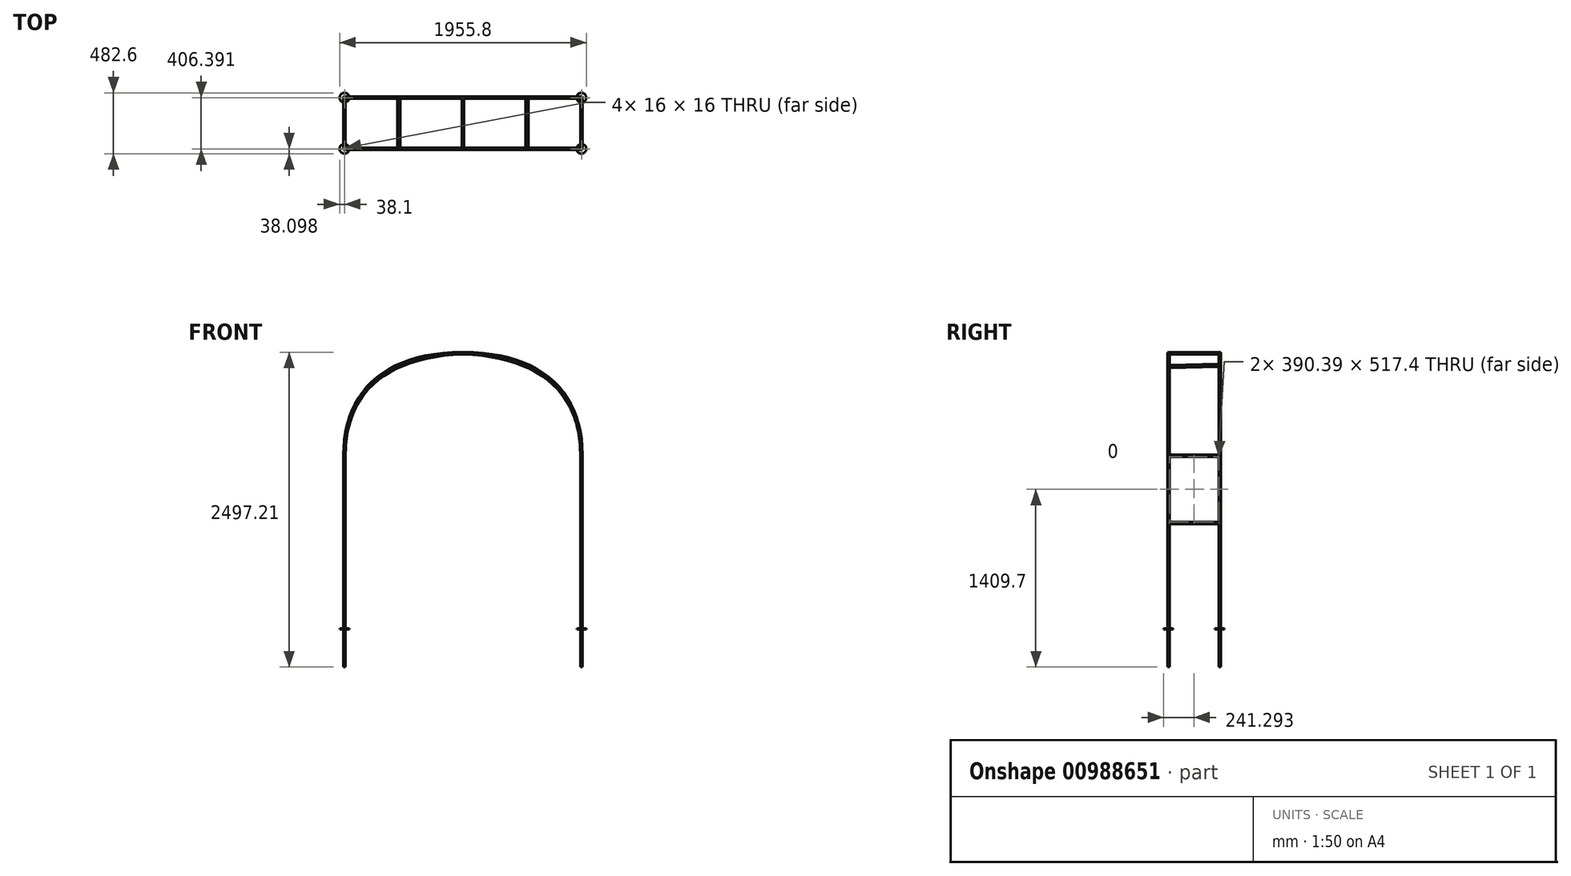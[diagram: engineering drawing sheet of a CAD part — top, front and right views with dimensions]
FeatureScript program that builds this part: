
annotation { "Feature Type Name" : "Feature", "Feature Type Description" : "" }
export const myFeature = defineFeature(function(context is Context, id is Id, definition is map)
    precondition{}
    {
        {
            var Q0;
            Q0=qCreatedBy(makeId("Right.planeOp"),FACE);
            cPlane(context, id + "F0", {"entities" : qUnion([Q0]), "cplaneType" : CPlaneType.OFFSET, "offset" : 939.8 * mm, "oppositeDirection" : true, "width" : 152.4 * mm, "height" : 152.4 * mm});
        }
        {
            var Q0;
            Q0=qCreatedBy(id+"F0.planeOp",FACE);
            var sketch = newSketch(context, id + "F1", { "sketchPlane" : qUnion([Q0])});
            skLineSegment(sketch, "E0", {"start": v(0, 0) * mm, "end": v(-203.2, 0) * mm, "construction": true});
            skLineSegment(sketch, "E1", {"start": v(0, 0) * mm, "end": v(203.2, 0) * mm, "construction": true});
            skLineSegment(sketch, "E2", {"start": v(203.2, 0) * mm, "end": v(203.2, 2184.4) * mm, "construction": true});
            skLineSegment(sketch, "E3", {"start": v(203.2, 2184.4) * mm, "end": v(-203.2, 2184.4) * mm, "construction": true});
            skLineSegment(sketch, "E4", {"start": v(-203.2, 2184.4) * mm, "end": v(-203.2, 0) * mm, "construction": true});
            skSolve(sketch);
        }
        {
            var Q0;
            Q0=qCreatedBy(makeId("Right.planeOp"),FACE);
            var sketch = newSketch(context, id + "F2", { "sketchPlane" : qUnion([Q0])});
            skPoint(sketch, "E5.0", {"position": v(0, 2184.4) * mm});
            skLineSegment(sketch, "E6.0", {"start": v(-203.2, 2184.4) * mm, "end": v(-203.2, 0) * mm, "construction": true});
            skLineSegment(sketch, "E7.0", {"start": v(203.2, 0) * mm, "end": v(203.2, 2184.4) * mm, "construction": true});
            skSolve(sketch);
        }
        {
            var Q0;
            Q0=qCreatedBy(id+"F0.planeOp",FACE);
            var sketch = newSketch(context, id + "F3", { "sketchPlane" : qUnion([Q0])});
            skLineSegment(sketch, "E8", {"start": v(-203.2, 0) * mm, "end": v(-203.2, 1371.6) * mm});
            skLineSegment(sketch, "E9", {"start": v(203.19, 0) * mm, "end": v(203.19, 1371.6) * mm});
            skSolve(sketch);
        }
        {
            var Q0;
            Q0=sQuery(id+"F1.wireOp",EDGE,"E4");
            cPlane(context, id + "F4", {"entities" : qUnion([Q0]), "cplaneType" : CPlaneType.LINE_ANGLE, "offset" : 25.4 * mm, "angle" : 90 * degree, "width" : 152.4 * mm, "height" : 152.4 * mm});
        }
        {
            var Q0;
            Q0=sQuery(id+"F1.wireOp",EDGE,"E2");
            cPlane(context, id + "F5", {"entities" : qUnion([Q0]), "cplaneType" : CPlaneType.LINE_ANGLE, "offset" : 25.4 * mm, "angle" : 90 * degree, "width" : 152.4 * mm, "height" : 152.4 * mm});
        }
        {
            var Q0;
            Q0=qCreatedBy(id+"F4.planeOp",FACE);
            var sketch = newSketch(context, id + "F6", { "sketchPlane" : qUnion([Q0])});
            skFitSpline(sketch, "E10", {"points": [v(939.8, 1371.6) * mm, v(0, 2184.4) * mm], "startDerivative": vector(-1.02, 1524) * mm, "endDerivative": vector(-1828.8, 68.52) * mm});
            skLineSegment(sketch, "E11", {"start": v(609.6, 2161.56) * mm, "end": v(0, 2184.4) * mm, "construction": true});
            skLineSegment(sketch, "E12", {"start": v(939.8, 1371.6) * mm, "end": v(939.46, 1879.6) * mm, "construction": true});
            skSolve(sketch);
        }
        {
            var Q0;
            Q0=qCreatedBy(id+"F5.planeOp",FACE);
            var sketch = newSketch(context, id + "F7", { "sketchPlane" : qUnion([Q0])});
            skFitSpline(sketch, "E13", {"points": [v(939.8, 1371.6) * mm, v(0, 2184.4) * mm], "startDerivative": vector(3.24, 1524) * mm, "endDerivative": vector(-1828.8, -5.61) * mm});
            skLineSegment(sketch, "E14", {"start": v(939.8, 1371.6) * mm, "end": v(940.88, 1879.6) * mm, "construction": true});
            skLineSegment(sketch, "E15", {"start": v(0, 2184.4) * mm, "end": v(609.6, 2186.27) * mm, "construction": true});
            skSolve(sketch);
        }
        {
            var Q0;
            Q0=qCreatedBy(makeId("Top.planeOp"),FACE);
            var sketch = newSketch(context, id + "F8", { "sketchPlane" : qUnion([Q0])});
            skLineSegment(sketch, "E16.bottom", {"start": v(-947.8, -195.2) * mm, "end": v(-931.8, -195.2) * mm});
            skLineSegment(sketch, "E16.top", {"start": v(-947.8, -211.2) * mm, "end": v(-931.8, -211.2) * mm});
            skLineSegment(sketch, "E16.left", {"start": v(-947.8, -195.2) * mm, "end": v(-947.8, -211.2) * mm});
            skLineSegment(sketch, "E16.right", {"start": v(-931.8, -195.2) * mm, "end": v(-931.8, -211.2) * mm});
            skLineSegment(sketch, "E17", {"start": v(-947.8, -195.2) * mm, "end": v(-931.8, -211.2) * mm, "construction": true});
            skPoint(sketch, "E18", {"position": v(-939.8, -203.2) * mm});
            skLineSegment(sketch, "E19.bottom", {"start": v(-931.8, 211.19) * mm, "end": v(-947.8, 211.19) * mm});
            skLineSegment(sketch, "E19.top", {"start": v(-931.8, 195.19) * mm, "end": v(-947.8, 195.19) * mm});
            skLineSegment(sketch, "E19.left", {"start": v(-931.8, 211.19) * mm, "end": v(-931.8, 195.19) * mm});
            skLineSegment(sketch, "E19.right", {"start": v(-947.8, 211.19) * mm, "end": v(-947.8, 195.19) * mm});
            skLineSegment(sketch, "E20", {"start": v(-931.8, 211.19) * mm, "end": v(-947.8, 195.19) * mm, "construction": true});
            skPoint(sketch, "E21", {"position": v(-939.8, 203.19) * mm});
            skSolve(sketch);
        }
        {
            var Q0;
            Q0=makeQuery(id+"F8.imprint","IMPRINT",FACE,{"disambiguationData":[TD([[makeQuery(id+"F8.imprint","IMPRINT",EDGE,{"derivedFrom":sQuery(id+"F8.wireOp",EDGE,"E19.bottom")}),1.0]])]});
            var Q1;
            Q1=sQuery(id+"F3.wireOp",EDGE,"E9");
            sweep(context, id + "F9", {"profiles" : qUnion([Q0]), "path" : qUnion([Q1])});
        }
        {
            var Q0;
            Q0=makeQuery(id+"F8.imprint","IMPRINT",FACE,{"disambiguationData":[TD([[makeQuery(id+"F8.imprint","IMPRINT",EDGE,{"derivedFrom":sQuery(id+"F8.wireOp",EDGE,"E16.bottom")}),-1.0]])]});
            var Q1;
            Q1=sQuery(id+"F3.wireOp",EDGE,"E8");
            sweep(context, id + "F10", {"profiles" : qUnion([Q0]), "path" : qUnion([Q1])});
        }
        {
            var Q0;
            Q0=makeQuery(id+"F10.opSweep","CAP_FACE",FACE,{"disambiguationData":[OSD([sQuery(id+"F3.wireOp",VERTEX,"E8.end"),sQuery(id+"F8.wireOp",EDGE,"dGPdL38b-pFhj-TtEV-cKe8-G57E5a3NYJfa")])],"isStart":false});
            var Q1;
            Q1=sQuery(id+"F6.wireOp",EDGE,"E10");
            sweep(context, id + "F11", {"operationType" : NewBodyOperationType.ADD, "profiles" : qUnion([Q0]), "path" : qUnion([Q1])});
        }
        {
            var Q0;
            Q0=qCreatedBy(id+"F0.planeOp",FACE);
            var sketch = newSketch(context, id + "F12", { "sketchPlane" : qUnion([Q0])});
            skLineSegment(sketch, "E22", {"start": v(203.19, 838.2) * mm, "end": v(-203.2, 838.2) * mm});
            skSolve(sketch);
        }
        {
            var Q0;
            Q0=qCreatedBy(id+"F0.planeOp",FACE);
            var sketch = newSketch(context, id + "F13", { "sketchPlane" : qUnion([Q0])});
            skLineSegment(sketch, "E23", {"start": v(-203.2, 1371.6) * mm, "end": v(203.19, 1371.6) * mm});
            skSolve(sketch);
        }
        {
            var Q0;
            Q0=makeQuery(id+"F9.opSweep","CAP_FACE",FACE,{"disambiguationData":[OSD([sQuery(id+"F3.wireOp",VERTEX,"E9.end"),sQuery(id+"F8.wireOp",EDGE,"A7kbO7hZ-qHPU-M1P2-TBv8-yGFhnXoMKm63")])],"isStart":false});
            var Q1;
            Q1=sQuery(id+"F7.wireOp",EDGE,"E13");
            sweep(context, id + "F14", {"operationType" : NewBodyOperationType.ADD, "profiles" : qUnion([Q0]), "path" : qUnion([Q1])});
        }
        {
            var Q0;
            Q0=qCreatedBy(makeId("Right.planeOp"),FACE);
            var sketch = newSketch(context, id + "F15", { "sketchPlane" : qUnion([Q0])});
            skLineSegment(sketch, "E24", {"start": v(-203.2, 2184.4) * mm, "end": v(203.2, 2184.4) * mm});
            skSolve(sketch);
        }
        {
            var Q0;
            Q0=qCreatedBy(id+"F4.planeOp",FACE);
            var sketch = newSketch(context, id + "F16", { "sketchPlane" : qUnion([Q0])});
            skCircle(sketch, "E25", {"center": v(939.8, 838.2) * mm, "radius": 8 * mm});
            skCircle(sketch, "E26", {"center": v(939.8, 1371.6) * mm, "radius": 8 * mm});
            skLineSegment(sketch, "E27.bottom", {"start": v(947.8, 830.2) * mm, "end": v(931.8, 830.2) * mm});
            skLineSegment(sketch, "E27.top", {"start": v(947.8, 846.2) * mm, "end": v(931.8, 846.2) * mm});
            skLineSegment(sketch, "E27.left", {"start": v(947.8, 830.2) * mm, "end": v(947.8, 846.2) * mm});
            skLineSegment(sketch, "E27.right", {"start": v(931.8, 830.2) * mm, "end": v(931.8, 846.2) * mm});
            skLineSegment(sketch, "E28", {"start": v(947.8, 830.2) * mm, "end": v(931.8, 846.2) * mm, "construction": true});
            skLineSegment(sketch, "E29.bottom", {"start": v(947.8, 1379.6) * mm, "end": v(931.8, 1379.6) * mm});
            skLineSegment(sketch, "E29.top", {"start": v(947.8, 1363.6) * mm, "end": v(931.8, 1363.6) * mm});
            skLineSegment(sketch, "E29.left", {"start": v(947.8, 1379.6) * mm, "end": v(947.8, 1363.6) * mm});
            skLineSegment(sketch, "E29.right", {"start": v(931.8, 1379.6) * mm, "end": v(931.8, 1363.6) * mm});
            skLineSegment(sketch, "E30", {"start": v(947.8, 1363.6) * mm, "end": v(931.8, 1379.6) * mm, "construction": true});
            skSolve(sketch);
        }
        {
            var Q0;
            Q0=makeQuery(id+"F16.imprint","IMPRINT",FACE,{"disambiguationData":[TD([[makeQuery(id+"F16.imprint","IMPRINT",EDGE,{"derivedFrom":sQuery(id+"F16.wireOp",EDGE,"E25")}),1.0]])]});
            var Q1;
            Q1=sQuery(id+"F12.wireOp",EDGE,"E22");
            sweep(context, id + "F17", {"operationType" : NewBodyOperationType.ADD, "profiles" : qUnion([Q0]), "path" : qUnion([Q1])});
        }
        {
            var Q0;
            Q0=qSketchRegion(id+"F16",true);
            var Q1;
            Q1=sQuery(id+"F13.wireOp",EDGE,"E23");
            sweep(context, id + "F18", {"operationType" : NewBodyOperationType.ADD, "profiles" : qUnion([Q0]), "path" : qUnion([Q1])});
        }
        {
            var Q0;
            Q0=qCreatedBy(id+"F4.planeOp",FACE);
            var sketch = newSketch(context, id + "F19", { "sketchPlane" : qUnion([Q0])});
            skLineSegment(sketch, "E31", {"start": v(8, 2176.4) * mm, "end": v(-8, 2192.4) * mm, "construction": true});
            skPoint(sketch, "E32", {"position": v(0, 2184.4) * mm});
            skLineSegment(sketch, "E33.bottom", {"start": v(8, 2176.4) * mm, "end": v(-8, 2176.4) * mm});
            skLineSegment(sketch, "E33.top", {"start": v(8, 2192.4) * mm, "end": v(-8, 2192.4) * mm});
            skLineSegment(sketch, "E33.left", {"start": v(8, 2176.4) * mm, "end": v(8, 2192.4) * mm});
            skLineSegment(sketch, "E33.right", {"start": v(-8, 2176.4) * mm, "end": v(-8, 2192.4) * mm});
            skSolve(sketch);
        }
        {
            var Q0;
            Q0=makeQuery(id+"F19.imprint","IMPRINT",FACE,{"disambiguationData":[TD([[makeQuery(id+"F19.imprint","IMPRINT",EDGE,{"derivedFrom":sQuery(id+"F19.wireOp",EDGE,"E33.bottom")}),-1.0]])]});
            var Q1;
            Q1=sQuery(id+"F15.wireOp",EDGE,"E24");
            sweep(context, id + "F20", {"operationType" : NewBodyOperationType.ADD, "profiles" : qUnion([Q0]), "path" : qUnion([Q1])});
        }
        {
            var Q0;
            Q0=qCreatedBy(makeId("Right.planeOp"),FACE);
            cPlane(context, id + "F21", {"entities" : qUnion([Q0]), "cplaneType" : CPlaneType.OFFSET, "offset" : 508 * mm, "oppositeDirection" : true, "width" : 152.4 * mm, "height" : 152.4 * mm});
        }
        {
            var Q0;
            Q0=qCreatedBy(id+"F21.planeOp",FACE);
            var sketch = newSketch(context, id + "F22", { "sketchPlane" : qUnion([Q0])});
            skLineSegment(sketch, "E34", {"start": v(-203.2, 2079.37) * mm, "end": v(203.05, 2090.49) * mm});
            skSolve(sketch);
        }
        {
            var Q0;
            Q0=qCreatedBy(id+"F4.planeOp",FACE);
            var sketch = newSketch(context, id + "F23", { "sketchPlane" : qUnion([Q0])});
            skLineSegment(sketch, "E35.bottom", {"start": v(518.22, 2082.18) * mm, "end": v(503.72, 2088.94) * mm});
            skLineSegment(sketch, "E35.top", {"start": v(511.46, 2067.67) * mm, "end": v(496.96, 2074.44) * mm});
            skLineSegment(sketch, "E35.left", {"start": v(518.22, 2082.18) * mm, "end": v(511.46, 2067.67) * mm});
            skLineSegment(sketch, "E35.right", {"start": v(503.72, 2088.94) * mm, "end": v(496.96, 2074.44) * mm});
            skPoint(sketch, "E36", {"position": v(507.59, 2078.3) * mm});
            skLineSegment(sketch, "E37", {"start": v(511.46, 2067.67) * mm, "end": v(503.72, 2088.94) * mm, "construction": true});
            skSolve(sketch);
        }
        {
            var Q0;
            Q0=qSketchRegion(id+"F23",true);
            var Q1;
            Q1=sQuery(id+"F22.wireOp",EDGE,"E34");
            sweep(context, id + "F24", {"operationType" : NewBodyOperationType.ADD, "profiles" : qUnion([Q0]), "path" : qUnion([Q1])});
        }
        {
            var Q0;
            Q0=qCreatedBy(makeId("Top.planeOp"),FACE);
            var sketch = newSketch(context, id + "F25", { "sketchPlane" : qUnion([Q0])});
            skCircle(sketch, "E38", {"center": v(-939.8, -203.2) * mm, "radius": 38.1 * mm});
            skCircle(sketch, "E39", {"center": v(-939.8, 203.2) * mm, "radius": 38.1 * mm});
            skSolve(sketch);
        }
        {
            var Q0;
            Q0=qSketchRegion(id+"F25",true);
            extrude(context, id + "F26", {"entities" : qUnion([Q0]), "operationType" : NewBodyOperationType.ADD, "oppositeDirection" : true, "depth" : 6.35 * mm, "offsetDistance" : 25.4 * mm});
        }
        {
            var Q0;
            Q0=makeQuery(id+"F8.imprint","IMPRINT",FACE,{"disambiguationData":[TD([[makeQuery(id+"F8.imprint","IMPRINT",EDGE,{"derivedFrom":sQuery(id+"F8.wireOp",EDGE,"E16.bottom")}),-1.0]])]});
            extrude(context, id + "F27", {"entities" : qUnion([Q0]), "operationType" : NewBodyOperationType.ADD, "oppositeDirection" : true, "depth" : 304.8 * mm, "offsetDistance" : 25.4 * mm});
        }
        {
            var Q0;
            Q0=makeQuery(id+"F8.imprint","IMPRINT",FACE,{"disambiguationData":[TD([[makeQuery(id+"F8.imprint","IMPRINT",EDGE,{"derivedFrom":sQuery(id+"F8.wireOp",EDGE,"E19.bottom")}),1.0]])]});
            extrude(context, id + "F28", {"entities" : qUnion([Q0]), "operationType" : NewBodyOperationType.ADD, "oppositeDirection" : true, "depth" : 304.8 * mm, "offsetDistance" : 25.4 * mm});
        }
        {
            var Q0;
            Q0=makeQuery(id+"F9.opSweep","SWEPT_BODY",BODY,{"disambiguationData":[OSD([sQuery(id+"F3.wireOp",EDGE,"E9"),sQuery(id+"F8.wireOp",EDGE,"A7kbO7hZ-qHPU-M1P2-TBv8-yGFhnXoMKm63")])]});
            var Q1;
            Q1=qCreatedBy(makeId("Right.planeOp"),FACE);
            mirror(context, id + "F29", {"operationType" : NewBodyOperationType.ADD, "entities" : qUnion([Q0]), "mirrorPlane" : qUnion([Q1])});
        }
    });
